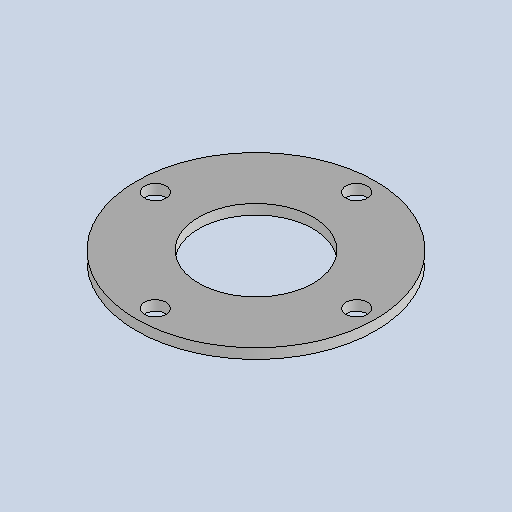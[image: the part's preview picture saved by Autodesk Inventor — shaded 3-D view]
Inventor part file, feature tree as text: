
AUTODESK INVENTOR PART (.ipt)
format: ipt  version: 2025.1 (Build 291241020, 241B)  size: 146,432 bytes
history: native  units: mm
features: other x3, sketch x2, sheet_metal_op x1, pattern_circular x1
ambient origin geometry x8: Origin, YZ Plane, XZ Plane, XY Plane, X Axis, Y Axis, Z Axis, Center Point
bodies: Body1 (feature_tree)
feature tree (7):
  sheet_metal_op  "Face2"
  pattern_circular  "Circular Pattern1"  [2 undecoded]
  sketch  "Sketch2"  dims[d14=8.0mm]
  other  "Plate2"
  sketch  "Sketch3"  dims[d15=17.0mm d17=8.0mm d18=0.0mm d19=40.0mm d20=360.0deg d25=91.0mm d27=190.0mm d28=160.0mm]
  other  "Cut1"
  other  "Definition1"
note: 2 required parameter values undecoded (feature->parameter linkage not recoverable at this tier; creation-order binding heuristic only, values carry confidence <= 0.55)
